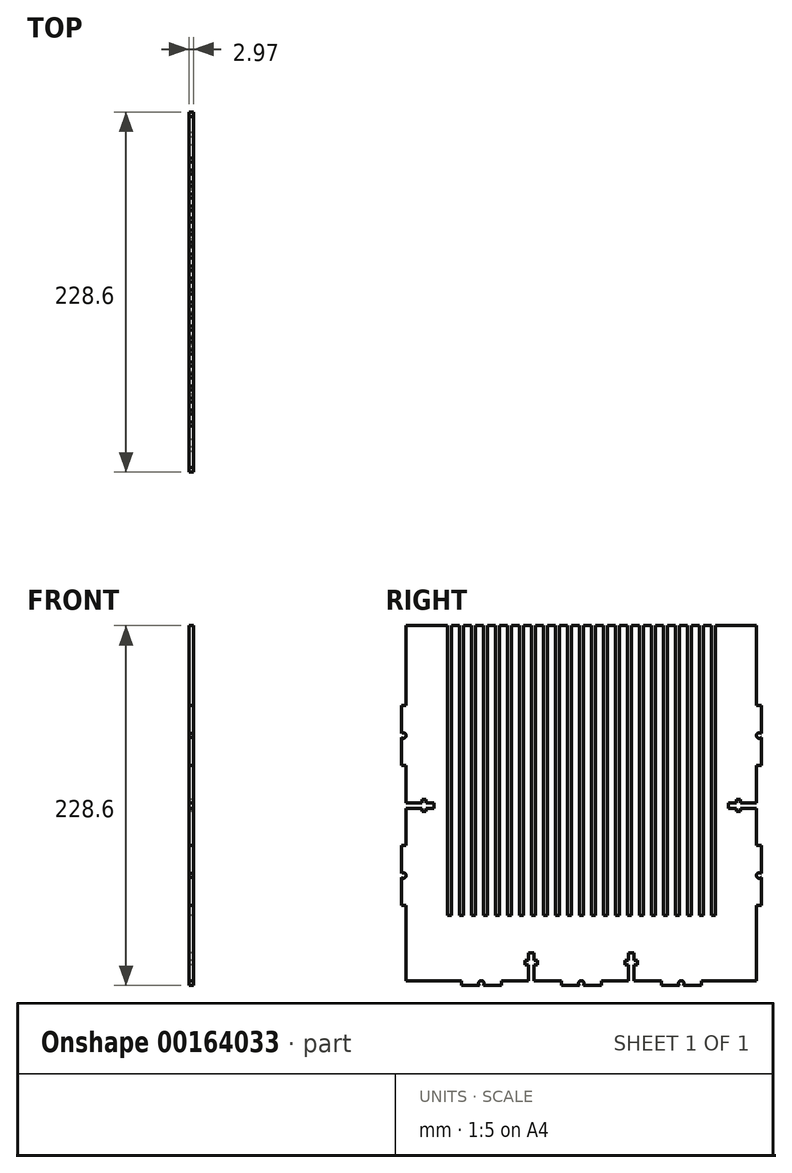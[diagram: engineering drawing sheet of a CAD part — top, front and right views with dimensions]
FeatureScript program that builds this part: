
annotation { "Feature Type Name" : "Feature", "Feature Type Description" : "" }
export const myFeature = defineFeature(function(context is Context, id is Id, definition is map)
    precondition{}
    {
        {
            var Q0;
            Q0=qCreatedBy(makeId("Right.planeOp"),FACE);
            var sketch = newSketch(context, id + "F0", { "sketchPlane" : qUnion([Q0])});
            skLineSegment(sketch, "E0.bottom", {"start": v(114.3, -114.3) * mm, "end": v(-114.3, -114.3) * mm});
            skLineSegment(sketch, "E0.top", {"start": v(114.3, 114.3) * mm, "end": v(-114.3, 114.3) * mm});
            skLineSegment(sketch, "E0.left", {"start": v(114.3, -114.3) * mm, "end": v(114.3, 114.3) * mm});
            skLineSegment(sketch, "E0.right", {"start": v(-114.3, -114.3) * mm, "end": v(-114.3, 114.3) * mm});
            skPoint(sketch, "E0.middle", {"position": v(0, 0) * mm});
            skLineSegment(sketch, "E1.bottom", {"start": v(-114.3, -63.5) * mm, "end": v(-111.33, -63.5) * mm});
            skLineSegment(sketch, "E1.top", {"start": v(-114.3, -114.3) * mm, "end": v(-111.33, -114.3) * mm});
            skLineSegment(sketch, "E1.left", {"start": v(-114.3, -63.5) * mm, "end": v(-114.3, -114.3) * mm});
            skLineSegment(sketch, "E1.right", {"start": v(-111.33, -63.5) * mm, "end": v(-111.33, -114.3) * mm});
            skLineSegment(sketch, "E2.0.1.0", {"start": v(-114.3, 25.4) * mm, "end": v(-114.3, -25.4) * mm});
            skLineSegment(sketch, "E2.0.1.1", {"start": v(-111.33, 25.4) * mm, "end": v(-111.33, 1.77) * mm});
            skLineSegment(sketch, "E2.0.1.2", {"start": v(-114.3, -25.4) * mm, "end": v(-111.33, -25.4) * mm});
            skLineSegment(sketch, "E2.0.1.3", {"start": v(-114.3, 25.4) * mm, "end": v(-111.33, 25.4) * mm});
            skLineSegment(sketch, "E2.0.2.0", {"start": v(-114.3, 114.3) * mm, "end": v(-114.3, 63.5) * mm});
            skLineSegment(sketch, "E2.0.2.1", {"start": v(-111.33, 114.3) * mm, "end": v(-111.33, 63.5) * mm});
            skLineSegment(sketch, "E2.0.2.2", {"start": v(-114.3, 63.5) * mm, "end": v(-111.33, 63.5) * mm});
            skLineSegment(sketch, "E2.0.2.3", {"start": v(-114.3, 114.3) * mm, "end": v(-111.33, 114.3) * mm});
            skLineSegment(sketch, "E2.direction1", {"start": v(-114.3, -114.3) * mm, "end": v(-88.9, -114.3) * mm, "construction": true});
            skLineSegment(sketch, "E2.direction2", {"start": v(-114.3, -114.3) * mm, "end": v(-114.3, -25.4) * mm, "construction": true});
            skArc(sketch, "E3", {"start": v(-114.3, -45.7) * mm, "mid": v(-111.25, -44.45) * mm, "end": v(-114.3, -43.2) * mm});
            skArc(sketch, "E4.0.1.0", {"start": v(-114.3, 43.2) * mm, "mid": v(-111.25, 44.45) * mm, "end": v(-114.3, 45.7) * mm});
            skLineSegment(sketch, "E4.direction1", {"start": v(-113.03, -44.45) * mm, "end": v(-87.63, -44.45) * mm, "construction": true});
            skLineSegment(sketch, "E4.direction2", {"start": v(-113.03, -44.45) * mm, "end": v(-113.03, 44.45) * mm, "construction": true});
            skLineSegment(sketch, "E5.MirrorCS", {"start": v(114.3, -114.3) * mm, "end": v(111.33, -114.3) * mm});
            skLineSegment(sketch, "E6.MirrorCS", {"start": v(114.3, 114.3) * mm, "end": v(111.33, 114.3) * mm});
            skArc(sketch, "E7.MirrorCS", {"start": v(114.3, -45.7) * mm, "mid": v(111.25, -44.45) * mm, "end": v(114.3, -43.2) * mm});
            skLineSegment(sketch, "E8.MirrorCS", {"start": v(114.3, -25.4) * mm, "end": v(111.33, -25.4) * mm});
            skArc(sketch, "E9.MirrorCS", {"start": v(114.3, 43.2) * mm, "mid": v(111.25, 44.45) * mm, "end": v(114.3, 45.7) * mm});
            skLineSegment(sketch, "E10.MirrorCS", {"start": v(114.3, 25.4) * mm, "end": v(111.33, 25.4) * mm});
            skLineSegment(sketch, "E11.MirrorCS", {"start": v(114.3, -63.5) * mm, "end": v(111.33, -63.5) * mm});
            skLineSegment(sketch, "E12.MirrorCS", {"start": v(114.3, 63.5) * mm, "end": v(111.33, 63.5) * mm});
            skLineSegment(sketch, "E13.MirrorCS", {"start": v(114.3, 25.4) * mm, "end": v(114.3, -25.4) * mm});
            skLineSegment(sketch, "E14.MirrorCS", {"start": v(114.3, -63.5) * mm, "end": v(114.3, -114.3) * mm});
            skLineSegment(sketch, "E15.MirrorCS", {"start": v(114.3, 114.3) * mm, "end": v(114.3, 63.5) * mm});
            skLineSegment(sketch, "E16.MirrorCS", {"start": v(111.33, 25.4) * mm, "end": v(111.33, 1.77) * mm});
            skLineSegment(sketch, "E17.MirrorCS", {"start": v(111.33, -63.5) * mm, "end": v(111.33, -114.3) * mm});
            skLineSegment(sketch, "E18.MirrorCS", {"start": v(113.03, -44.45) * mm, "end": v(113.03, 44.45) * mm, "construction": true});
            skLineSegment(sketch, "E19.MirrorCS", {"start": v(111.33, 114.3) * mm, "end": v(111.33, 63.5) * mm});
            skLineSegment(sketch, "E20.MirrorCS", {"start": v(114.3, -114.3) * mm, "end": v(114.3, -25.4) * mm, "construction": true});
            skLineSegment(sketch, "E21.bottom", {"start": v(-76.2, -114.3) * mm, "end": v(-114.3, -114.3) * mm});
            skLineSegment(sketch, "E21.top", {"start": v(-76.2, -111.33) * mm, "end": v(-114.3, -111.33) * mm});
            skLineSegment(sketch, "E21.left", {"start": v(-76.2, -114.3) * mm, "end": v(-76.2, -111.33) * mm});
            skLineSegment(sketch, "E21.right", {"start": v(-114.3, -114.3) * mm, "end": v(-114.3, -111.33) * mm});
            skLineSegment(sketch, "E22.1.0.0", {"start": v(-12.7, -114.3) * mm, "end": v(-50.8, -114.3) * mm});
            skLineSegment(sketch, "E22.1.0.1", {"start": v(-50.8, -114.3) * mm, "end": v(-25.4, -114.3) * mm, "construction": true});
            skLineSegment(sketch, "E22.1.0.2", {"start": v(-12.7, -111.33) * mm, "end": v(-29.98, -111.33) * mm});
            skLineSegment(sketch, "E22.1.0.3", {"start": v(-50.8, -114.3) * mm, "end": v(-47.83, -114.3) * mm});
            skLineSegment(sketch, "E22.1.0.4", {"start": v(-50.8, -114.3) * mm, "end": v(-50.8, -111.33) * mm});
            skLineSegment(sketch, "E22.1.0.5", {"start": v(-12.7, -114.3) * mm, "end": v(-12.7, -111.33) * mm});
            skLineSegment(sketch, "E22.2.0.0", {"start": v(50.8, -114.3) * mm, "end": v(12.7, -114.3) * mm});
            skLineSegment(sketch, "E22.2.0.1", {"start": v(12.7, -114.3) * mm, "end": v(38.1, -114.3) * mm, "construction": true});
            skLineSegment(sketch, "E22.2.0.2", {"start": v(50.8, -111.33) * mm, "end": v(33.52, -111.33) * mm});
            skLineSegment(sketch, "E22.2.0.3", {"start": v(12.7, -114.3) * mm, "end": v(15.67, -114.3) * mm});
            skLineSegment(sketch, "E22.2.0.4", {"start": v(12.7, -114.3) * mm, "end": v(12.7, -111.33) * mm});
            skLineSegment(sketch, "E22.2.0.5", {"start": v(50.8, -114.3) * mm, "end": v(50.8, -111.33) * mm});
            skLineSegment(sketch, "E22.3.0.0", {"start": v(114.3, -114.3) * mm, "end": v(76.2, -114.3) * mm});
            skLineSegment(sketch, "E22.3.0.1", {"start": v(76.2, -114.3) * mm, "end": v(101.6, -114.3) * mm, "construction": true});
            skLineSegment(sketch, "E22.3.0.2", {"start": v(114.3, -111.33) * mm, "end": v(76.2, -111.33) * mm});
            skLineSegment(sketch, "E22.3.0.3", {"start": v(76.2, -114.3) * mm, "end": v(79.17, -114.3) * mm});
            skLineSegment(sketch, "E22.3.0.4", {"start": v(76.2, -114.3) * mm, "end": v(76.2, -111.33) * mm});
            skLineSegment(sketch, "E22.3.0.5", {"start": v(114.3, -114.3) * mm, "end": v(114.3, -111.33) * mm});
            skLineSegment(sketch, "E22.direction1", {"start": v(-114.3, -114.3) * mm, "end": v(-50.8, -114.3) * mm, "construction": true});
            skLineSegment(sketch, "E23.bottom", {"start": v(-33.52, -93.5) * mm, "end": v(-29.98, -93.5) * mm});
            skLineSegment(sketch, "E23.top", {"start": v(-33.52, -114.3) * mm, "end": v(-29.98, -114.3) * mm});
            skLineSegment(sketch, "E23.left", {"start": v(-33.52, -93.5) * mm, "end": v(-33.52, -98.53) * mm});
            skLineSegment(sketch, "E23.right", {"start": v(-29.98, -93.5) * mm, "end": v(-29.98, -98.53) * mm});
            skPoint(sketch, "E24", {"position": v(-31.75, -114.3) * mm});
            skLineSegment(sketch, "E25", {"start": v(-31.75, -114.33) * mm, "end": v(-31.75, -114.3) * mm, "construction": true});
            skPoint(sketch, "E25.endSnap0", {"position": v(-31.75, -93.5) * mm});
            skLineSegment(sketch, "E26.bottom", {"start": v(-27.86, -101.17) * mm, "end": v(-29.98, -101.17) * mm});
            skLineSegment(sketch, "E26.top", {"start": v(-27.86, -98.53) * mm, "end": v(-29.98, -98.53) * mm});
            skLineSegment(sketch, "E26.left", {"start": v(-27.86, -101.17) * mm, "end": v(-27.86, -98.53) * mm});
            skLineSegment(sketch, "E26.right", {"start": v(-35.64, -101.17) * mm, "end": v(-35.64, -98.53) * mm});
            skPoint(sketch, "E26.middle", {"position": v(-31.75, -99.85) * mm});
            skLineSegment(sketch, "E27", {"start": v(-31.75, -114.3) * mm, "end": v(-31.75, -84.3) * mm, "construction": true});
            skLineSegment(sketch, "E28.1.0.0", {"start": v(33.52, -93.5) * mm, "end": v(33.52, -98.53) * mm});
            skLineSegment(sketch, "E28.1.0.1", {"start": v(29.98, -93.5) * mm, "end": v(33.52, -93.5) * mm});
            skLineSegment(sketch, "E28.1.0.2", {"start": v(29.98, -93.5) * mm, "end": v(29.98, -98.53) * mm});
            skLineSegment(sketch, "E28.1.0.3", {"start": v(29.98, -114.3) * mm, "end": v(33.52, -114.3) * mm});
            skLineSegment(sketch, "E28.1.0.4", {"start": v(35.64, -98.53) * mm, "end": v(33.52, -98.53) * mm});
            skLineSegment(sketch, "E28.1.0.5", {"start": v(27.86, -101.17) * mm, "end": v(27.86, -98.53) * mm});
            skLineSegment(sketch, "E28.1.0.6", {"start": v(35.64, -101.17) * mm, "end": v(33.52, -101.17) * mm});
            skLineSegment(sketch, "E28.1.0.7", {"start": v(35.64, -101.17) * mm, "end": v(35.64, -98.53) * mm});
            skLineSegment(sketch, "E28.1.0.8", {"start": v(31.75, -114.3) * mm, "end": v(31.75, -84.3) * mm, "construction": true});
            skLineSegment(sketch, "E28.direction1", {"start": v(-29.98, -114.3) * mm, "end": v(33.52, -114.3) * mm, "construction": true});
            skLineSegment(sketch, "E29.trimOffspring", {"start": v(-33.52, -111.33) * mm, "end": v(-50.8, -111.33) * mm});
            skLineSegment(sketch, "E30.trimOffspring", {"start": v(-29.98, -101.17) * mm, "end": v(-29.98, -111.33) * mm});
            skLineSegment(sketch, "E31.trimOffspring", {"start": v(-33.52, -98.53) * mm, "end": v(-35.64, -98.53) * mm});
            skLineSegment(sketch, "E32.trimOffspring", {"start": v(-33.52, -101.17) * mm, "end": v(-33.52, -111.33) * mm});
            skLineSegment(sketch, "E33.trimOffspring", {"start": v(-33.52, -101.17) * mm, "end": v(-35.64, -101.17) * mm});
            skLineSegment(sketch, "E34.trimOffspring", {"start": v(29.98, -111.33) * mm, "end": v(12.7, -111.33) * mm});
            skLineSegment(sketch, "E35.trimOffspring", {"start": v(33.52, -101.17) * mm, "end": v(33.52, -111.33) * mm});
            skLineSegment(sketch, "E36.trimOffspring", {"start": v(29.98, -98.53) * mm, "end": v(27.86, -98.53) * mm});
            skLineSegment(sketch, "E37.trimOffspring", {"start": v(29.98, -101.17) * mm, "end": v(29.98, -111.33) * mm});
            skLineSegment(sketch, "E38.trimOffspring", {"start": v(29.98, -101.17) * mm, "end": v(27.86, -101.17) * mm});
            skLineSegment(sketch, "E39.top", {"start": v(-111.33, -1.77) * mm, "end": v(-101.17, -1.77) * mm});
            skLineSegment(sketch, "E39.left", {"start": v(-114.3, 1.77) * mm, "end": v(-114.3, -1.77) * mm});
            skLineSegment(sketch, "E39.right", {"start": v(-93.5, 1.77) * mm, "end": v(-93.5, -1.77) * mm});
            skPoint(sketch, "E40", {"position": v(-114.3, 0) * mm});
            skPoint(sketch, "E41.endSnap0", {"position": v(-93.5, 0) * mm});
            skLineSegment(sketch, "E42.bottom", {"start": v(-98.53, -3.89) * mm, "end": v(-101.17, -3.89) * mm});
            skLineSegment(sketch, "E42.top", {"start": v(-98.53, 3.89) * mm, "end": v(-101.17, 3.89) * mm});
            skLineSegment(sketch, "E42.left", {"start": v(-98.53, -3.89) * mm, "end": v(-98.53, -1.77) * mm});
            skLineSegment(sketch, "E42.right", {"start": v(-101.17, -3.89) * mm, "end": v(-101.17, -1.77) * mm});
            skPoint(sketch, "E42.middle", {"position": v(-99.85, 0) * mm});
            skLineSegment(sketch, "E43", {"start": v(-114.3, 0) * mm, "end": v(-93.5, 0) * mm, "construction": true});
            skLineSegment(sketch, "E44.trimOffspring", {"start": v(-98.53, 1.77) * mm, "end": v(-98.53, 3.89) * mm});
            skLineSegment(sketch, "E45.trimOffspring", {"start": v(-98.53, 1.77) * mm, "end": v(-93.5, 1.77) * mm});
            skLineSegment(sketch, "E46.trimOffspring", {"start": v(-101.17, 1.77) * mm, "end": v(-101.17, 3.89) * mm});
            skLineSegment(sketch, "E47.trimOffspring", {"start": v(-98.53, -1.77) * mm, "end": v(-93.5, -1.77) * mm});
            skLineSegment(sketch, "E48.trimOffspring", {"start": v(-111.33, -1.77) * mm, "end": v(-111.33, -25.4) * mm});
            skLineSegment(sketch, "E49.trimOffspring", {"start": v(-111.33, 1.77) * mm, "end": v(-101.17, 1.77) * mm});
            skLineSegment(sketch, "E50.MirrorCS", {"start": v(98.53, 1.77) * mm, "end": v(98.53, 3.89) * mm});
            skLineSegment(sketch, "E51.MirrorCS", {"start": v(101.17, 1.77) * mm, "end": v(101.17, 3.89) * mm});
            skLineSegment(sketch, "E52.MirrorCS", {"start": v(93.5, 1.77) * mm, "end": v(93.5, -1.77) * mm});
            skLineSegment(sketch, "E53.MirrorCS", {"start": v(114.3, 1.77) * mm, "end": v(114.3, -1.77) * mm});
            skLineSegment(sketch, "E54.MirrorCS", {"start": v(114.3, 0) * mm, "end": v(93.5, 0) * mm, "construction": true});
            skLineSegment(sketch, "E55.MirrorCS", {"start": v(111.33, 1.77) * mm, "end": v(101.17, 1.77) * mm});
            skPoint(sketch, "E56.MirrorP", {"position": v(99.85, 0) * mm});
            skLineSegment(sketch, "E57.MirrorCS", {"start": v(111.33, -1.77) * mm, "end": v(101.17, -1.77) * mm});
            skPoint(sketch, "E58.MirrorP", {"position": v(93.5, 0) * mm});
            skLineSegment(sketch, "E59.MirrorCS", {"start": v(101.17, -3.89) * mm, "end": v(101.17, -1.77) * mm});
            skLineSegment(sketch, "E60.MirrorCS", {"start": v(98.53, 3.89) * mm, "end": v(101.17, 3.89) * mm});
            skLineSegment(sketch, "E61.MirrorCS", {"start": v(98.53, -1.77) * mm, "end": v(93.5, -1.77) * mm});
            skLineSegment(sketch, "E62.MirrorCS", {"start": v(98.53, 1.77) * mm, "end": v(93.5, 1.77) * mm});
            skPoint(sketch, "E63.MirrorP", {"position": v(114.3, 0) * mm});
            skLineSegment(sketch, "E64.MirrorCS", {"start": v(98.53, -3.89) * mm, "end": v(101.17, -3.89) * mm});
            skLineSegment(sketch, "E65.MirrorCS", {"start": v(98.53, -3.89) * mm, "end": v(98.53, -1.77) * mm});
            skLineSegment(sketch, "E66.trimOffspring", {"start": v(111.33, -1.77) * mm, "end": v(111.33, -25.4) * mm});
            skArc(sketch, "E67", {"start": v(-62.26, -114.3) * mm, "mid": v(-63.5, -111.25) * mm, "end": v(-64.74, -114.3) * mm});
            skArc(sketch, "E68.1.0.0", {"start": v(1.24, -114.3) * mm, "mid": v(0, -111.25) * mm, "end": v(-1.24, -114.3) * mm});
            skArc(sketch, "E68.2.0.0", {"start": v(64.74, -114.3) * mm, "mid": v(63.5, -111.25) * mm, "end": v(62.26, -114.3) * mm});
            skLineSegment(sketch, "E68.direction1", {"start": v(-63.5, -113.03) * mm, "end": v(0, -113.03) * mm, "construction": true});
            skLineSegment(sketch, "E69.bottom", {"start": v(-85.1, 114.3) * mm, "end": v(-82.55, 114.3) * mm});
            skLineSegment(sketch, "E69.top", {"start": v(-85.1, -69.85) * mm, "end": v(-82.55, -69.85) * mm});
            skLineSegment(sketch, "E69.left", {"start": v(-85.1, 114.3) * mm, "end": v(-85.1, -69.85) * mm});
            skLineSegment(sketch, "E69.right", {"start": v(-82.55, 114.3) * mm, "end": v(-82.55, -69.85) * mm});
            skLineSegment(sketch, "E70.1.0.0", {"start": v(-77.47, 114.3) * mm, "end": v(-77.47, -69.85) * mm});
            skLineSegment(sketch, "E70.1.0.2", {"start": v(-74.93, 114.3) * mm, "end": v(-74.93, -69.85) * mm});
            skLineSegment(sketch, "E70.1.0.3", {"start": v(-77.47, 114.3) * mm, "end": v(-74.93, 114.3) * mm});
            skLineSegment(sketch, "E70.1.0.4", {"start": v(-77.47, -69.85) * mm, "end": v(-74.93, -69.85) * mm});
            skLineSegment(sketch, "E70.2.0.0", {"start": v(-69.85, 114.3) * mm, "end": v(-69.85, -69.85) * mm});
            skLineSegment(sketch, "E70.2.0.2", {"start": v(-67.31, 114.3) * mm, "end": v(-67.31, -69.85) * mm});
            skLineSegment(sketch, "E70.2.0.3", {"start": v(-69.85, 114.3) * mm, "end": v(-67.31, 114.3) * mm});
            skLineSegment(sketch, "E70.2.0.4", {"start": v(-69.85, -69.85) * mm, "end": v(-67.31, -69.85) * mm});
            skLineSegment(sketch, "E70.3.0.0", {"start": v(-62.23, 114.3) * mm, "end": v(-62.23, -69.85) * mm});
            skLineSegment(sketch, "E70.3.0.2", {"start": v(-59.7, 114.3) * mm, "end": v(-59.7, -69.85) * mm});
            skLineSegment(sketch, "E70.3.0.3", {"start": v(-62.23, 114.3) * mm, "end": v(-59.7, 114.3) * mm});
            skLineSegment(sketch, "E70.3.0.4", {"start": v(-62.23, -69.85) * mm, "end": v(-59.7, -69.85) * mm});
            skLineSegment(sketch, "E70.4.0.0", {"start": v(-54.61, 114.3) * mm, "end": v(-54.61, -69.85) * mm});
            skLineSegment(sketch, "E70.4.0.2", {"start": v(-52.07, 114.3) * mm, "end": v(-52.07, -69.85) * mm});
            skLineSegment(sketch, "E70.4.0.3", {"start": v(-54.61, 114.3) * mm, "end": v(-52.07, 114.3) * mm});
            skLineSegment(sketch, "E70.4.0.4", {"start": v(-54.61, -69.85) * mm, "end": v(-52.07, -69.85) * mm});
            skLineSegment(sketch, "E70.5.0.0", {"start": v(-47, 114.3) * mm, "end": v(-47, -69.85) * mm});
            skLineSegment(sketch, "E70.5.0.2", {"start": v(-44.45, 114.3) * mm, "end": v(-44.45, -69.85) * mm});
            skLineSegment(sketch, "E70.5.0.3", {"start": v(-47, 114.3) * mm, "end": v(-44.45, 114.3) * mm});
            skLineSegment(sketch, "E70.5.0.4", {"start": v(-47, -69.85) * mm, "end": v(-44.45, -69.85) * mm});
            skLineSegment(sketch, "E70.6.0.0", {"start": v(-39.37, 114.3) * mm, "end": v(-39.37, -69.85) * mm});
            skLineSegment(sketch, "E70.6.0.2", {"start": v(-36.83, 114.3) * mm, "end": v(-36.83, -69.85) * mm});
            skLineSegment(sketch, "E70.6.0.3", {"start": v(-39.37, 114.3) * mm, "end": v(-36.83, 114.3) * mm});
            skLineSegment(sketch, "E70.6.0.4", {"start": v(-39.37, -69.85) * mm, "end": v(-36.83, -69.85) * mm});
            skLineSegment(sketch, "E70.7.0.0", {"start": v(-31.75, 114.3) * mm, "end": v(-31.75, -69.85) * mm});
            skLineSegment(sketch, "E70.7.0.2", {"start": v(-29.21, 114.3) * mm, "end": v(-29.21, -69.85) * mm});
            skLineSegment(sketch, "E70.7.0.3", {"start": v(-31.75, 114.3) * mm, "end": v(-29.21, 114.3) * mm});
            skLineSegment(sketch, "E70.7.0.4", {"start": v(-31.75, -69.85) * mm, "end": v(-29.21, -69.85) * mm});
            skLineSegment(sketch, "E70.8.0.0", {"start": v(-24.13, 114.3) * mm, "end": v(-24.13, -69.85) * mm});
            skLineSegment(sketch, "E70.8.0.2", {"start": v(-21.6, 114.3) * mm, "end": v(-21.59, -69.85) * mm});
            skLineSegment(sketch, "E70.8.0.3", {"start": v(-24.13, 114.3) * mm, "end": v(-21.6, 114.3) * mm});
            skLineSegment(sketch, "E70.8.0.4", {"start": v(-24.13, -69.85) * mm, "end": v(-21.59, -69.85) * mm});
            skLineSegment(sketch, "E70.9.0.0", {"start": v(-16.51, 114.3) * mm, "end": v(-16.51, -69.85) * mm});
            skLineSegment(sketch, "E70.9.0.2", {"start": v(-13.97, 114.3) * mm, "end": v(-13.97, -69.85) * mm});
            skLineSegment(sketch, "E70.9.0.3", {"start": v(-16.51, 114.3) * mm, "end": v(-13.97, 114.3) * mm});
            skLineSegment(sketch, "E70.9.0.4", {"start": v(-16.5, -69.85) * mm, "end": v(-13.97, -69.85) * mm});
            skLineSegment(sketch, "E70.10.0.0", {"start": v(-8.9, 114.3) * mm, "end": v(-8.89, -69.85) * mm});
            skLineSegment(sketch, "E70.10.0.2", {"start": v(-6.35, 114.3) * mm, "end": v(-6.35, -69.85) * mm});
            skLineSegment(sketch, "E70.10.0.3", {"start": v(-8.9, 114.3) * mm, "end": v(-6.35, 114.3) * mm});
            skLineSegment(sketch, "E70.10.0.4", {"start": v(-8.89, -69.85) * mm, "end": v(-6.35, -69.85) * mm});
            skLineSegment(sketch, "E70.11.0.0", {"start": v(-1.27, 114.3) * mm, "end": v(-1.27, -69.85) * mm});
            skLineSegment(sketch, "E70.11.0.2", {"start": v(1.27, 114.3) * mm, "end": v(1.27, -69.85) * mm});
            skLineSegment(sketch, "E70.11.0.3", {"start": v(-1.27, 114.3) * mm, "end": v(1.27, 114.3) * mm});
            skLineSegment(sketch, "E70.11.0.4", {"start": v(-1.27, -69.85) * mm, "end": v(1.27, -69.85) * mm});
            skLineSegment(sketch, "E70.12.0.0", {"start": v(6.35, 114.3) * mm, "end": v(6.35, -69.85) * mm});
            skLineSegment(sketch, "E70.12.0.2", {"start": v(8.89, 114.3) * mm, "end": v(8.9, -69.85) * mm});
            skLineSegment(sketch, "E70.12.0.3", {"start": v(6.35, 114.3) * mm, "end": v(8.89, 114.3) * mm});
            skLineSegment(sketch, "E70.12.0.4", {"start": v(6.35, -69.85) * mm, "end": v(8.9, -69.85) * mm});
            skLineSegment(sketch, "E70.13.0.0", {"start": v(13.97, 114.3) * mm, "end": v(13.97, -69.85) * mm});
            skLineSegment(sketch, "E70.13.0.2", {"start": v(16.5, 114.3) * mm, "end": v(16.51, -69.85) * mm});
            skLineSegment(sketch, "E70.13.0.3", {"start": v(13.97, 114.3) * mm, "end": v(16.5, 114.3) * mm});
            skLineSegment(sketch, "E70.13.0.4", {"start": v(13.97, -69.85) * mm, "end": v(16.51, -69.85) * mm});
            skLineSegment(sketch, "E70.14.0.0", {"start": v(21.59, 114.3) * mm, "end": v(21.6, -69.85) * mm});
            skLineSegment(sketch, "E70.14.0.2", {"start": v(24.13, 114.3) * mm, "end": v(24.13, -69.85) * mm});
            skLineSegment(sketch, "E70.14.0.3", {"start": v(21.59, 114.3) * mm, "end": v(24.13, 114.3) * mm});
            skLineSegment(sketch, "E70.14.0.4", {"start": v(21.6, -69.85) * mm, "end": v(24.13, -69.85) * mm});
            skLineSegment(sketch, "E70.15.0.0", {"start": v(29.2, 114.3) * mm, "end": v(29.21, -69.85) * mm});
            skLineSegment(sketch, "E70.15.0.2", {"start": v(31.75, 114.3) * mm, "end": v(31.75, -69.85) * mm});
            skLineSegment(sketch, "E70.15.0.3", {"start": v(29.2, 114.3) * mm, "end": v(31.75, 114.3) * mm});
            skLineSegment(sketch, "E70.15.0.4", {"start": v(29.21, -69.85) * mm, "end": v(31.75, -69.85) * mm});
            skLineSegment(sketch, "E70.16.0.0", {"start": v(36.83, 114.3) * mm, "end": v(36.83, -69.85) * mm});
            skLineSegment(sketch, "E70.16.0.2", {"start": v(39.37, 114.3) * mm, "end": v(39.37, -69.85) * mm});
            skLineSegment(sketch, "E70.16.0.3", {"start": v(36.83, 114.3) * mm, "end": v(39.37, 114.3) * mm});
            skLineSegment(sketch, "E70.16.0.4", {"start": v(36.83, -69.85) * mm, "end": v(39.37, -69.85) * mm});
            skLineSegment(sketch, "E70.17.0.0", {"start": v(44.45, 114.3) * mm, "end": v(44.45, -69.85) * mm});
            skLineSegment(sketch, "E70.17.0.2", {"start": v(47, 114.3) * mm, "end": v(47, -69.85) * mm});
            skLineSegment(sketch, "E70.17.0.3", {"start": v(44.45, 114.3) * mm, "end": v(47, 114.3) * mm});
            skLineSegment(sketch, "E70.17.0.4", {"start": v(44.45, -69.85) * mm, "end": v(47, -69.85) * mm});
            skLineSegment(sketch, "E70.18.0.0", {"start": v(52.07, 114.3) * mm, "end": v(52.07, -69.85) * mm});
            skLineSegment(sketch, "E70.18.0.2", {"start": v(54.6, 114.3) * mm, "end": v(54.61, -69.85) * mm});
            skLineSegment(sketch, "E70.18.0.3", {"start": v(52.07, 114.3) * mm, "end": v(54.6, 114.3) * mm});
            skLineSegment(sketch, "E70.18.0.4", {"start": v(52.07, -69.85) * mm, "end": v(54.61, -69.85) * mm});
            skLineSegment(sketch, "E70.19.0.0", {"start": v(59.69, 114.3) * mm, "end": v(59.7, -69.85) * mm});
            skLineSegment(sketch, "E70.19.0.2", {"start": v(62.23, 114.3) * mm, "end": v(62.23, -69.85) * mm});
            skLineSegment(sketch, "E70.19.0.3", {"start": v(59.69, 114.3) * mm, "end": v(62.23, 114.3) * mm});
            skLineSegment(sketch, "E70.19.0.4", {"start": v(59.7, -69.85) * mm, "end": v(62.23, -69.85) * mm});
            skLineSegment(sketch, "E70.20.0.0", {"start": v(67.3, 114.3) * mm, "end": v(67.31, -69.85) * mm});
            skLineSegment(sketch, "E70.20.0.2", {"start": v(69.85, 114.3) * mm, "end": v(69.85, -69.85) * mm});
            skLineSegment(sketch, "E70.20.0.3", {"start": v(67.3, 114.3) * mm, "end": v(69.85, 114.3) * mm});
            skLineSegment(sketch, "E70.20.0.4", {"start": v(67.31, -69.85) * mm, "end": v(69.85, -69.85) * mm});
            skLineSegment(sketch, "E70.21.0.0", {"start": v(74.93, 114.3) * mm, "end": v(74.93, -69.85) * mm});
            skLineSegment(sketch, "E70.21.0.2", {"start": v(77.47, 114.3) * mm, "end": v(77.47, -69.85) * mm});
            skLineSegment(sketch, "E70.21.0.3", {"start": v(74.93, 114.3) * mm, "end": v(77.47, 114.3) * mm});
            skLineSegment(sketch, "E70.21.0.4", {"start": v(74.93, -69.85) * mm, "end": v(77.47, -69.85) * mm});
            skLineSegment(sketch, "E70.22.0.0", {"start": v(82.55, 114.3) * mm, "end": v(82.55, -69.85) * mm});
            skLineSegment(sketch, "E70.22.0.2", {"start": v(85.1, 114.3) * mm, "end": v(85.1, -69.85) * mm});
            skLineSegment(sketch, "E70.22.0.3", {"start": v(82.55, 114.3) * mm, "end": v(85.1, 114.3) * mm});
            skLineSegment(sketch, "E70.22.0.4", {"start": v(82.55, -69.85) * mm, "end": v(85.1, -69.85) * mm});
            skLineSegment(sketch, "E70.direction1", {"start": v(-85.1, -69.85) * mm, "end": v(-77.47, -69.85) * mm, "construction": true});
            skSolve(sketch);
        }
        {
            var Q0;
            Q0=makeQuery(id+"F0.imprint","IMPRINT",FACE,{"disambiguationData":[TD([[makeQuery(id+"F0.imprint","IMPRINT",EDGE,{"derivedFrom":sQuery(id+"F0.wireOp",EDGE,"E0.top")}),1.0]])]});
            extrude(context, id + "F1", {"entities" : qUnion([Q0]), "depth" : 2.97 * mm});
        }
    });
